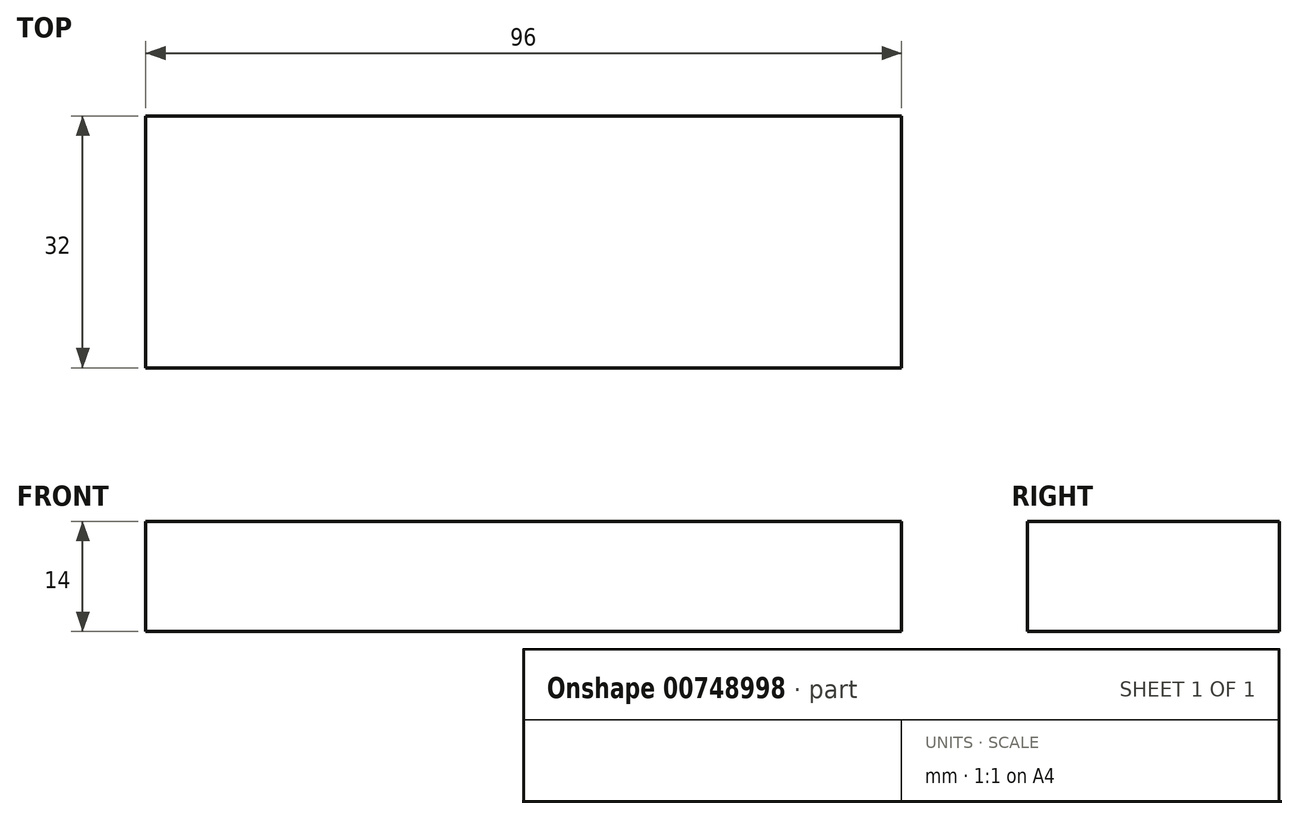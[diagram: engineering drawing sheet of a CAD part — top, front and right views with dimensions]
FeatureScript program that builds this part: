
annotation { "Feature Type Name" : "Feature", "Feature Type Description" : "" }
export const myFeature = defineFeature(function(context is Context, id is Id, definition is map)
    precondition{}
    {
        {
            var Q0;
            Q0=qCreatedBy(makeId("Top.planeOp"),FACE);
            var sketch = newSketch(context, id + "F0", { "sketchPlane" : qUnion([Q0])});
            skLineSegment(sketch, "E0.bottom", {"start": v(-54.36, 42.53) * mm, "end": v(41.64, 42.53) * mm});
            skLineSegment(sketch, "E0.top", {"start": v(-54.36, 10.53) * mm, "end": v(41.64, 10.53) * mm});
            skLineSegment(sketch, "E0.left", {"start": v(-54.36, 42.53) * mm, "end": v(-54.36, 10.53) * mm});
            skLineSegment(sketch, "E0.right", {"start": v(41.64, 42.53) * mm, "end": v(41.64, 10.53) * mm});
            skSolve(sketch);
        }
        {
            var Q0;
            Q0 = qSketchRegion(id + "F0", true);
            extrude(context, id + "F1", {"entities" : qUnion([Q0]), "depth" : 14 * mm, "offsetDistance" : 25 * mm});
        }
    });
